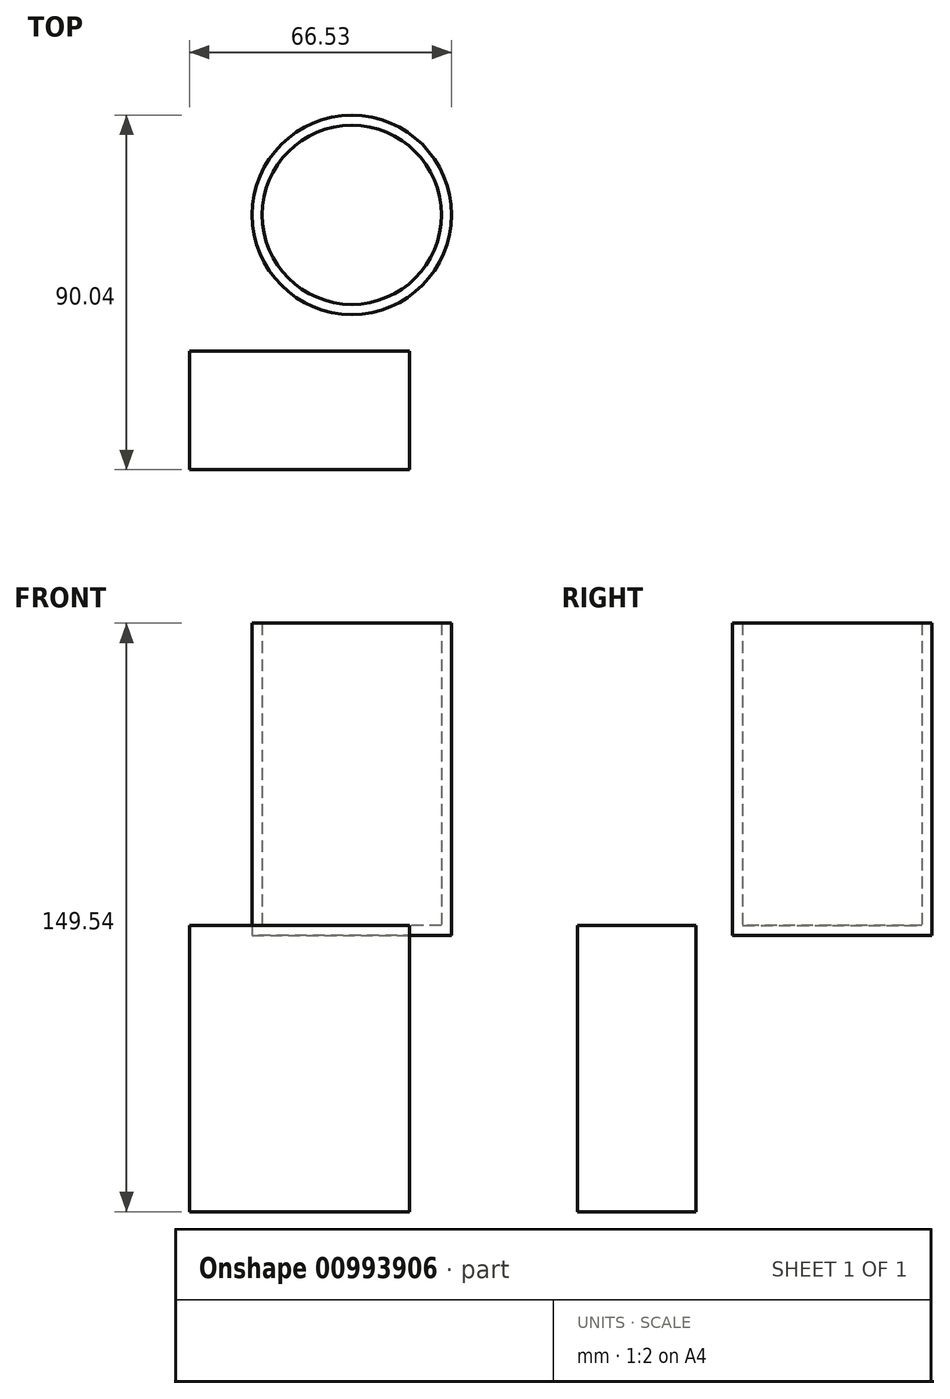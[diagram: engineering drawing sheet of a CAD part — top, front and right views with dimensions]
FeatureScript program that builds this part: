
annotation { "Feature Type Name" : "Feature", "Feature Type Description" : "" }
export const myFeature = defineFeature(function(context is Context, id is Id, definition is map)
    precondition{}
    {
        {
            var Q0;
            Q0=qCreatedBy(makeId("Top.planeOp"),FACE);
            var sketch = newSketch(context, id + "F0", { "sketchPlane" : qUnion([Q0])});
            skLineSegment(sketch, "E0.bottom", {"start": v(0, 0) * mm, "end": v(55.94, 0) * mm});
            skLineSegment(sketch, "E0.top", {"start": v(0, -30.13) * mm, "end": v(55.94, -30.13) * mm});
            skLineSegment(sketch, "E0.left", {"start": v(0, 0) * mm, "end": v(0, -30.13) * mm});
            skLineSegment(sketch, "E0.right", {"start": v(55.94, 0) * mm, "end": v(55.94, -30.13) * mm});
            skSolve(sketch);
        }
        {
            var Q0;
            Q0=makeQuery(id+"F0.imprint","IMPRINT",FACE,{"disambiguationData":[TD([[makeQuery(id+"F0.imprint","IMPRINT",EDGE,{"derivedFrom":sQuery(id+"F0.wireOp",EDGE,"E0.bottom")}),-1.0]])]});
            extrude(context, id + "F1", {"entities" : qUnion([Q0]), "depth" : 72.74 * mm, "offsetDistance" : 25.4 * mm});
        }
        {
            var Q0;
            Q0=makeQuery(id+"F1.opExtrude","CAP_FACE",FACE,{"disambiguationData":[OSD([sQuery(id+"F0.wireOp",EDGE,"E0.bottom"),sQuery(id+"F0.wireOp",EDGE,"E0.top"),sQuery(id+"F0.wireOp",EDGE,"E0.left"),sQuery(id+"F0.wireOp",EDGE,"E0.right")])],"isStart":false});
            var sketch = newSketch(context, id + "F2", { "sketchPlane" : qUnion([Q0])});
            skCircle(sketch, "E1", {"center": v(41.22, 34.6) * mm, "radius": 22.76 * mm});
            skSolve(sketch);
        }
        {
            var Q0;
            Q0=makeQuery(id+"F2.imprint","IMPRINT",FACE,{"disambiguationData":[TD([[makeQuery(id+"F2.imprint","IMPRINT",EDGE,{"derivedFrom":sQuery(id+"F2.wireOp",EDGE,"E1")}),1.0]])]});
            extrude(context, id + "F3", {"entities" : qUnion([Q0]), "depth" : 76.8 * mm, "offsetDistance" : 25.4 * mm});
        }
        {
            var Q0;
            Q0=makeQuery(id+"F3.opExtrude","CAP_FACE",FACE,{"disambiguationData":[OSD([sQuery(id+"F2.wireOp",EDGE,"E1")])],"isStart":false});
            shell(context, id + "F4", {"entities" : qUnion([Q0]), "thickness" : 2.54 * mm, "oppositeDirection" : true});
        }
    });
